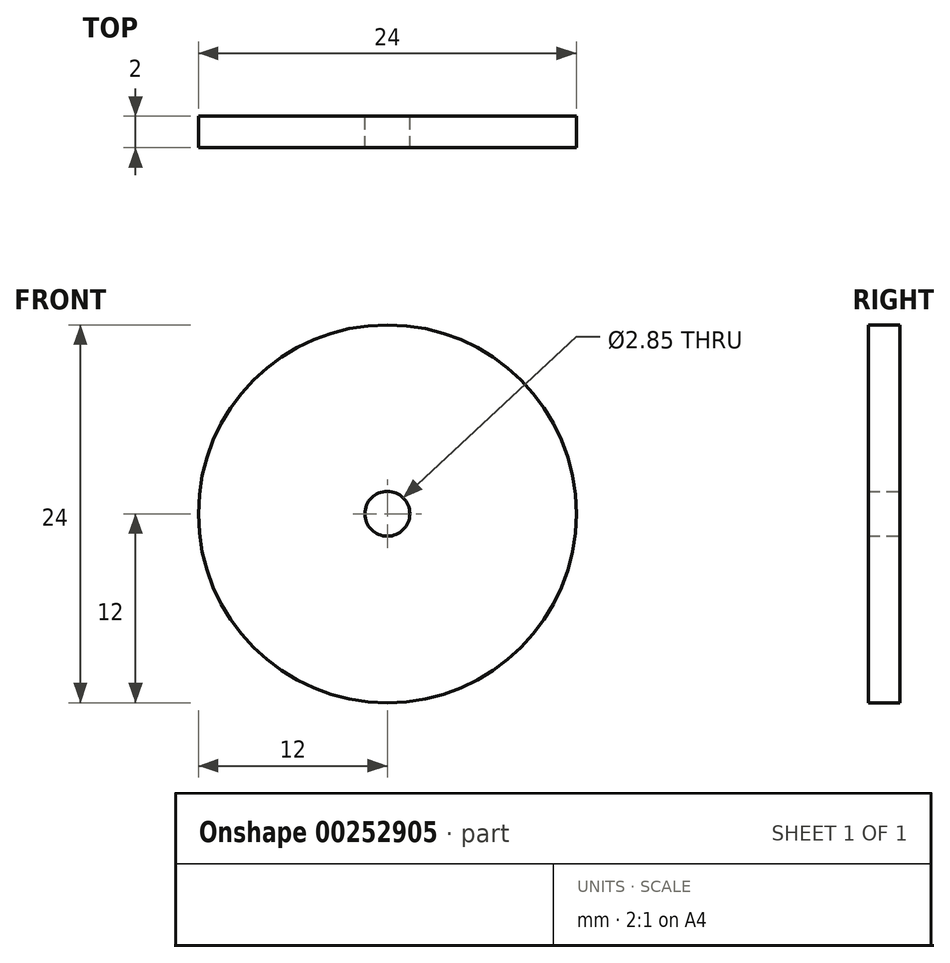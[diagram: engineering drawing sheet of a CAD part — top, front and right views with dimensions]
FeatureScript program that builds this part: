
annotation { "Feature Type Name" : "Feature", "Feature Type Description" : "" }
export const myFeature = defineFeature(function(context is Context, id is Id, definition is map)
    precondition{}
    {
        {
            var Q0;
            Q0=qCreatedBy(makeId("Front.planeOp"),FACE);
            var sketch = newSketch(context, id + "F0", { "sketchPlane" : qUnion([Q0])});
            skCircle(sketch, "E0", {"center": v(0, 0) * mm, "radius": 12 * mm});
            skCircle(sketch, "E1", {"center": v(0, 0) * mm, "radius": 1.43 * mm});
            skSolve(sketch);
        }
        {
            var Q0;
            Q0=makeQuery(id+"F0.imprint","IMPRINT",FACE,{"disambiguationData":[TD([[makeQuery(id+"F0.imprint","IMPRINT",EDGE,{"derivedFrom":sQuery(id+"F0.wireOp",EDGE,"E0")}),1.0]])]});
            extrude(context, id + "F1", {"entities" : qUnion([Q0]), "depth" : 2 * mm});
        }
    });
